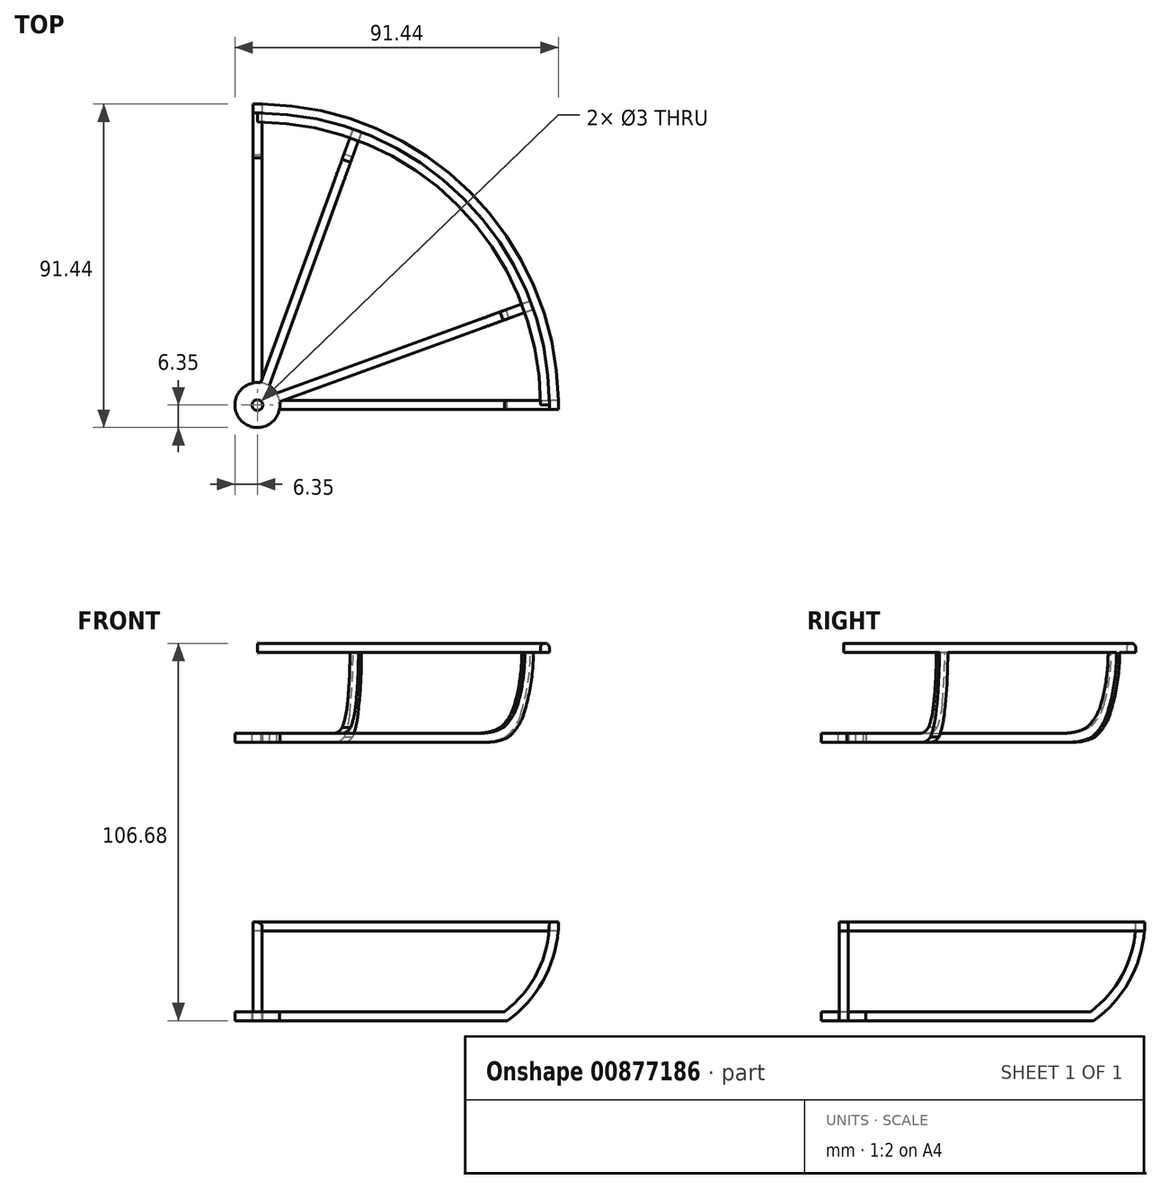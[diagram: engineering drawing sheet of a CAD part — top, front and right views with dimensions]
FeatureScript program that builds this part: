
annotation { "Feature Type Name" : "Feature", "Feature Type Description" : "" }
export const myFeature = defineFeature(function(context is Context, id is Id, definition is map)
    precondition{}
    {
        {
            var Q0;
            Q0=qCreatedBy(makeId("Front.planeOp"),FACE);
            var sketch = newSketch(context, id + "F0", { "sketchPlane" : qUnion([Q0])});
            skLineSegment(sketch, "E0", {"start": v(0, 0) * mm, "end": v(69.85, 0) * mm});
            skLineSegment(sketch, "E1.bottom", {"start": v(69.85, 0) * mm, "end": v(82.55, 0) * mm, "construction": true});
            skLineSegment(sketch, "E1.top", {"start": v(69.85, 25.4) * mm, "end": v(82.55, 25.4) * mm, "construction": true});
            skLineSegment(sketch, "E1.left", {"start": v(69.85, 0) * mm, "end": v(69.85, 25.4) * mm, "construction": true});
            skLineSegment(sketch, "E1.right", {"start": v(82.55, 0) * mm, "end": v(82.55, 25.4) * mm, "construction": true});
            skArc(sketch, "E2", {"start": v(69.85, 0) * mm, "mid": v(79.2, 11.2) * mm, "end": v(82.55, 25.4) * mm});
            skArc(sketch, "E3.0", {"start": v(70.68, -2.54) * mm, "mid": v(81.27, 9.68) * mm, "end": v(85.1, 25.4) * mm});
            skLineSegment(sketch, "E3.1", {"start": v(0, -2.54) * mm, "end": v(70.68, -2.54) * mm});
            skLineSegment(sketch, "E4", {"start": v(82.55, 25.4) * mm, "end": v(85.1, 25.4) * mm});
            skLineSegment(sketch, "E5", {"start": v(0, 0) * mm, "end": v(0, -2.54) * mm});
            skSolve(sketch);
        }
        {
            var Q0;
            Q0=qSketchRegion(id+"F0",true);
            extrude(context, id + "F1", {"entities" : qUnion([Q0]), "depth" : 2.54 * mm, "offsetDistance" : 25.4 * mm, "symmetric" : true});
        }
        {
            var Q0;
            Q0=qCreatedBy(makeId("Right.planeOp"),FACE);
            var sketch = newSketch(context, id + "F2", { "sketchPlane" : qUnion([Q0])});
            skLineSegment(sketch, "E6", {"start": v(0, 0) * mm, "end": v(69.85, 0) * mm});
            skLineSegment(sketch, "E7.bottom", {"start": v(69.85, 0) * mm, "end": v(82.55, 0) * mm, "construction": true});
            skLineSegment(sketch, "E7.top", {"start": v(69.85, 25.4) * mm, "end": v(82.55, 25.4) * mm, "construction": true});
            skLineSegment(sketch, "E7.left", {"start": v(69.85, 0) * mm, "end": v(69.85, 25.4) * mm, "construction": true});
            skLineSegment(sketch, "E7.right", {"start": v(82.55, 0) * mm, "end": v(82.55, 25.4) * mm, "construction": true});
            skArc(sketch, "E8", {"start": v(69.85, 0) * mm, "mid": v(79.2, 11.2) * mm, "end": v(82.55, 25.4) * mm});
            skArc(sketch, "E9.0", {"start": v(70.68, -2.54) * mm, "mid": v(81.27, 9.68) * mm, "end": v(85.1, 25.4) * mm});
            skLineSegment(sketch, "E9.1", {"start": v(0, -2.54) * mm, "end": v(70.68, -2.54) * mm});
            skLineSegment(sketch, "E10", {"start": v(82.55, 25.4) * mm, "end": v(85.1, 25.4) * mm});
            skLineSegment(sketch, "E11", {"start": v(0, 0) * mm, "end": v(0, -2.54) * mm});
            skSolve(sketch);
        }
        {
            var Q0;
            Q0=qSketchRegion(id+"F2",true);
            extrude(context, id + "F3", {"entities" : qUnion([Q0]), "operationType" : NewBodyOperationType.ADD, "depth" : 2.54 * mm, "offsetDistance" : 25.4 * mm, "symmetric" : true});
        }
        {
            var Q0;
            Q0=makeQuery(id+"F3.opExtrude","SWEPT_FACE",FACE,{"disambiguationData":[OSD([sQuery(id+"F2.wireOp",EDGE,"E10")])]});
            var sketch = newSketch(context, id + "F4", { "sketchPlane" : qUnion([Q0])});
            skPoint(sketch, "E12", {"position": v(0, 82.55) * mm});
            skLineSegment(sketch, "E13.bottom", {"start": v(0, 82.55) * mm, "end": v(82.55, 82.55) * mm, "construction": true});
            skLineSegment(sketch, "E13.top", {"start": v(0, 0) * mm, "end": v(82.55, 0) * mm, "construction": true});
            skLineSegment(sketch, "E13.left", {"start": v(0, 82.55) * mm, "end": v(0, 0) * mm, "construction": true});
            skLineSegment(sketch, "E13.right", {"start": v(82.55, 82.55) * mm, "end": v(82.55, 0) * mm, "construction": true});
            skArc(sketch, "E14", {"start": v(82.55, 0) * mm, "mid": v(58.37, 58.37) * mm, "end": v(0, 82.55) * mm});
            skArc(sketch, "E15.0", {"start": v(85.1, 0) * mm, "mid": v(60.17, 60.17) * mm, "end": v(0, 85.1) * mm});
            skLineSegment(sketch, "E16", {"start": v(82.55, 0) * mm, "end": v(83.82, 0) * mm, "construction": true});
            skLineSegment(sketch, "E17.bottom", {"start": v(85.1, -1.27) * mm, "end": v(82.55, -1.27) * mm});
            skLineSegment(sketch, "E17.top", {"start": v(85.1, 1.27) * mm, "end": v(82.55, 1.27) * mm});
            skLineSegment(sketch, "E17.left", {"start": v(85.1, -1.27) * mm, "end": v(85.1, 1.27) * mm});
            skLineSegment(sketch, "E17.right", {"start": v(82.55, -1.27) * mm, "end": v(82.55, 1.27) * mm});
            skPoint(sketch, "E17.middle", {"position": v(83.82, 0) * mm});
            skLineSegment(sketch, "E18", {"start": v(0, 82.55) * mm, "end": v(0, 83.82) * mm, "construction": true});
            skLineSegment(sketch, "E19.bottom", {"start": v(1.27, 85.1) * mm, "end": v(-1.27, 85.1) * mm});
            skLineSegment(sketch, "E19.top", {"start": v(1.27, 82.55) * mm, "end": v(-1.27, 82.55) * mm});
            skLineSegment(sketch, "E19.left", {"start": v(1.27, 85.1) * mm, "end": v(1.27, 82.55) * mm});
            skLineSegment(sketch, "E19.right", {"start": v(-1.27, 85.1) * mm, "end": v(-1.27, 82.55) * mm});
            skPoint(sketch, "E19.middle", {"position": v(0, 83.82) * mm});
            skSolve(sketch);
        }
        {
            var Q0;
            Q0=qSketchRegion(id+"F4",true);
            extrude(context, id + "F5", {"entities" : qUnion([Q0]), "operationType" : NewBodyOperationType.ADD, "oppositeDirection" : true, "depth" : 2.54 * mm, "offsetDistance" : 25.4 * mm});
        }
        {
            var Q0;
            Q0=qCreatedBy(makeId("Top.planeOp"),FACE);
            var sketch = newSketch(context, id + "F6", { "sketchPlane" : qUnion([Q0])});
            skCircle(sketch, "E20", {"center": v(0, 0) * mm, "radius": 6.35 * mm});
            skSolve(sketch);
        }
        {
            var Q0;
            Q0=qSketchRegion(id+"F6",true);
            extrude(context, id + "F7", {"entities" : qUnion([Q0]), "operationType" : NewBodyOperationType.ADD, "oppositeDirection" : true, "depth" : 2.54 * mm, "offsetDistance" : 25.4 * mm});
        }
        {
            var Q0;
            Q0=qCreatedBy(makeId("Top.planeOp"),FACE);
            var sketch = newSketch(context, id + "F8", { "sketchPlane" : qUnion([Q0])});
            skCircle(sketch, "E21", {"center": v(0, 0) * mm, "radius": 1.5 * mm});
            skSolve(sketch);
        }
        {
            var Q0;
            Q0=qSketchRegion(id+"F8",true);
            extrude(context, id + "F9", {"entities" : qUnion([Q0]), "operationType" : NewBodyOperationType.REMOVE, "oppositeDirection" : true, "depth" : 2.54 * mm, "offsetDistance" : 25.4 * mm});
        }
        {
            var Q0;
            Q0=makeQuery(id+"F5.boolean.opBoolean","MERGE",FACE,{"derivedFrom":[makeQuery(id+"F1.opExtrude","SWEPT_FACE",FACE,{"disambiguationData":[OSD([sQuery(id+"F0.wireOp",EDGE,"E4")])]}),makeQuery(id+"F3.opExtrude","SWEPT_FACE",FACE,{"disambiguationData":[OSD([sQuery(id+"F2.wireOp",EDGE,"E10")])]}),makeQuery(id+"F5.opExtrude","CAP_FACE",FACE,{"disambiguationData":[OSD([sQuery(id+"F4.wireOp",EDGE,"E14"),sQuery(id+"F4.wireOp",EDGE,"E15.0"),sQuery(id+"F4.wireOp",EDGE,"E17.bottom"),sQuery(id+"F4.wireOp",EDGE,"E17.top"),sQuery(id+"F4.wireOp",EDGE,"E17.left"),sQuery(id+"F4.wireOp",EDGE,"E17.right"),sQuery(id+"F4.wireOp",EDGE,"E19.bottom"),sQuery(id+"F4.wireOp",EDGE,"E19.top"),sQuery(id+"F4.wireOp",EDGE,"E19.left"),sQuery(id+"F4.wireOp",EDGE,"E19.right")])],"isStart":true})]});
            cPlane(context, id + "F10", {"entities" : qUnion([Q0]), "cplaneType" : CPlaneType.OFFSET, "offset" : 50.8 * mm, "width" : 152.4 * mm, "height" : 152.4 * mm});
        }
        {
            var Q0;
            Q0=qCreatedBy(id+"F10.planeOp",FACE);
            var sketch = newSketch(context, id + "F11", { "sketchPlane" : qUnion([Q0])});
            skCircle(sketch, "E22", {"center": v(0, 0) * mm, "radius": 6.35 * mm});
            skLineSegment(sketch, "E23", {"start": v(0, 0) * mm, "end": v(69.85, 0) * mm, "construction": true});
            skLineSegment(sketch, "E24", {"start": v(0, 0) * mm, "end": v(71.6, 26.06) * mm, "construction": true});
            skLineSegment(sketch, "E25", {"start": v(0, 0) * mm, "end": v(26.06, 71.6) * mm, "construction": true});
            skLineSegment(sketch, "E26.0", {"start": v(-2.12, -2.12) * mm, "end": v(72.04, 24.87) * mm});
            skLineSegment(sketch, "E26.1", {"start": v(-2.12, -2.12) * mm, "end": v(24.87, 72.04) * mm});
            skLineSegment(sketch, "E27.0", {"start": v(2.12, 2.12) * mm, "end": v(71.17, 27.26) * mm});
            skLineSegment(sketch, "E27.1", {"start": v(2.12, 2.12) * mm, "end": v(27.26, 71.17) * mm});
            skLineSegment(sketch, "E28", {"start": v(24.87, 72.04) * mm, "end": v(27.26, 71.17) * mm});
            skLineSegment(sketch, "E29", {"start": v(71.17, 27.26) * mm, "end": v(72.04, 24.87) * mm});
            skSolve(sketch);
        }
        {
            var Q0;
            Q0=qSketchRegion(id+"F11",true);
            extrude(context, id + "F12", {"entities" : qUnion([Q0]), "depth" : 2.54 * mm, "offsetDistance" : 25.4 * mm});
        }
        {
            var Q0;
            Q0=makeQuery(id+"F12.opExtrude","SWEPT_FACE",FACE,{"disambiguationData":[OSD([sQuery(id+"F11.wireOp",EDGE,"E26.0")])]});
            var sketch = newSketch(context, id + "F13", { "sketchPlane" : qUnion([Q0])});
            skLineSegment(sketch, "E30.bottom", {"start": v(76.2, 76.2) * mm, "end": v(82.55, 76.2) * mm, "construction": true});
            skLineSegment(sketch, "E30.top", {"start": v(76.2, 101.6) * mm, "end": v(82.55, 101.6) * mm, "construction": true});
            skLineSegment(sketch, "E30.left", {"start": v(76.2, 76.2) * mm, "end": v(76.2, 101.6) * mm, "construction": true});
            skLineSegment(sketch, "E30.right", {"start": v(82.55, 76.2) * mm, "end": v(82.55, 101.6) * mm, "construction": true});
            skArc(sketch, "E31", {"start": v(76.2, 76.2) * mm, "mid": v(80.94, 88.5) * mm, "end": v(82.55, 101.6) * mm});
            skArc(sketch, "E32.0", {"start": v(73.96, 77.4) * mm, "mid": v(78.47, 89.13) * mm, "end": v(80.01, 101.6) * mm});
            skLineSegment(sketch, "E33", {"start": v(73.96, 77.4) * mm, "end": v(76.2, 76.2) * mm});
            skLineSegment(sketch, "E34", {"start": v(82.55, 101.6) * mm, "end": v(80.01, 101.6) * mm});
            skSolve(sketch);
        }
        {
            var Q0;
            Q0=qSketchRegion(id+"F13",true);
            extrude(context, id + "F14", {"entities" : qUnion([Q0]), "operationType" : NewBodyOperationType.ADD, "oppositeDirection" : true, "depth" : 2.54 * mm, "offsetDistance" : 25.4 * mm});
        }
        {
            var Q0;
            Q0=makeQuery(id+"F12.opExtrude","SWEPT_FACE",FACE,{"disambiguationData":[OSD([sQuery(id+"F11.wireOp",EDGE,"E27.1")])]});
            var sketch = newSketch(context, id + "F15", { "sketchPlane" : qUnion([Q0])});
            skLineSegment(sketch, "E35.bottom", {"start": v(76.2, 76.2) * mm, "end": v(82.55, 76.2) * mm, "construction": true});
            skLineSegment(sketch, "E35.top", {"start": v(76.2, 101.6) * mm, "end": v(82.55, 101.6) * mm, "construction": true});
            skLineSegment(sketch, "E35.left", {"start": v(76.2, 76.2) * mm, "end": v(76.2, 101.6) * mm, "construction": true});
            skLineSegment(sketch, "E35.right", {"start": v(82.55, 76.2) * mm, "end": v(82.55, 101.6) * mm, "construction": true});
            skArc(sketch, "E36", {"start": v(76.2, 76.2) * mm, "mid": v(80.94, 88.5) * mm, "end": v(82.55, 101.6) * mm});
            skArc(sketch, "E37.0", {"start": v(73.96, 77.4) * mm, "mid": v(78.47, 89.13) * mm, "end": v(80.01, 101.6) * mm});
            skLineSegment(sketch, "E38", {"start": v(73.96, 77.4) * mm, "end": v(76.2, 76.2) * mm});
            skLineSegment(sketch, "E39", {"start": v(82.55, 101.6) * mm, "end": v(80.01, 101.6) * mm});
            skSolve(sketch);
        }
        {
            var Q0;
            Q0=qSketchRegion(id+"F15",true);
            extrude(context, id + "F16", {"entities" : qUnion([Q0]), "operationType" : NewBodyOperationType.ADD, "oppositeDirection" : true, "depth" : 2.54 * mm, "offsetDistance" : 25.4 * mm});
        }
        {
            var Q0;
            Q0=makeQuery(id+"F16.opExtrude","SWEPT_FACE",FACE,{"disambiguationData":[OSD([sQuery(id+"F15.wireOp",EDGE,"E39")])]});
            var sketch = newSketch(context, id + "F17", { "sketchPlane" : qUnion([Q0])});
            skLineSegment(sketch, "E40", {"start": v(0, 0) * mm, "end": v(0, 80.01) * mm, "construction": true});
            skLineSegment(sketch, "E41", {"start": v(0, 0) * mm, "end": v(80.01, 0) * mm, "construction": true});
            skArc(sketch, "E42", {"start": v(80.01, 0) * mm, "mid": v(56.58, 56.58) * mm, "end": v(0, 80.01) * mm});
            skArc(sketch, "E43.0", {"start": v(82.55, 0) * mm, "mid": v(58.37, 58.37) * mm, "end": v(0, 82.55) * mm});
            skLineSegment(sketch, "E44", {"start": v(0, 80.01) * mm, "end": v(0, 82.55) * mm});
            skLineSegment(sketch, "E45", {"start": v(80.01, 0) * mm, "end": v(82.55, 0) * mm});
            skSolve(sketch);
        }
        {
            var Q0;
            Q0=qSketchRegion(id+"F17",true);
            extrude(context, id + "F18", {"entities" : qUnion([Q0]), "operationType" : NewBodyOperationType.ADD, "depth" : 2.54 * mm, "offsetDistance" : 25.4 * mm});
        }
        {
            var Q0;
            Q0=makeQuery(id+"F12.opExtrude","CAP_FACE",FACE,{"disambiguationData":[OSD([sQuery(id+"F11.wireOp",EDGE,"E22"),sQuery(id+"F11.wireOp",EDGE,"E26.0"),sQuery(id+"F11.wireOp",EDGE,"E26.1"),sQuery(id+"F11.wireOp",EDGE,"E27.0"),sQuery(id+"F11.wireOp",EDGE,"E27.1"),sQuery(id+"F11.wireOp",EDGE,"E28"),sQuery(id+"F11.wireOp",EDGE,"E29")])],"isStart":false});
            var sketch = newSketch(context, id + "F19", { "sketchPlane" : qUnion([Q0])});
            skCircle(sketch, "E46", {"center": v(0, 0) * mm, "radius": 1.5 * mm});
            skSolve(sketch);
        }
        {
            var Q0;
            Q0=qSketchRegion(id+"F19",true);
            extrude(context, id + "F20", {"entities" : qUnion([Q0]), "operationType" : NewBodyOperationType.REMOVE, "oppositeDirection" : true, "depth" : 2.54 * mm, "offsetDistance" : 25.4 * mm});
        }
        {
            var Q0;
            Q0=makeQuery(id+"F14.boolean.opBoolean","INTERSECT",EDGE,{"derivedFrom":[makeQuery(id+"F12.opExtrude","CAP_FACE",FACE,{"disambiguationData":[OSD([sQuery(id+"F11.wireOp",EDGE,"E22"),sQuery(id+"F11.wireOp",EDGE,"E26.0"),sQuery(id+"F11.wireOp",EDGE,"E26.1"),sQuery(id+"F11.wireOp",EDGE,"E27.0"),sQuery(id+"F11.wireOp",EDGE,"E27.1"),sQuery(id+"F11.wireOp",EDGE,"E28"),sQuery(id+"F11.wireOp",EDGE,"E29")])],"isStart":false}),makeQuery(id+"F14.opExtrude","SWEPT_FACE",FACE,{"disambiguationData":[OSD([sQuery(id+"F13.wireOp",EDGE,"E32.0")])]})]});
            var Q1;
            Q1=makeQuery(id+"F16.boolean.opBoolean","INTERSECT",EDGE,{"derivedFrom":[makeQuery(id+"F12.opExtrude","CAP_FACE",FACE,{"disambiguationData":[OSD([sQuery(id+"F11.wireOp",EDGE,"E22"),sQuery(id+"F11.wireOp",EDGE,"E26.0"),sQuery(id+"F11.wireOp",EDGE,"E26.1"),sQuery(id+"F11.wireOp",EDGE,"E27.0"),sQuery(id+"F11.wireOp",EDGE,"E27.1"),sQuery(id+"F11.wireOp",EDGE,"E28"),sQuery(id+"F11.wireOp",EDGE,"E29")])],"isStart":false}),makeQuery(id+"F16.opExtrude","SWEPT_FACE",FACE,{"disambiguationData":[OSD([sQuery(id+"F15.wireOp",EDGE,"E37.0")])]})]});
            var Q2;
            {var subQ0=sQuery(id+"F11.wireOp",EDGE,"E28");Q2=makeQuery(id+"F16.boolean.opBoolean","MERGE",EDGE,{"derivedFrom":[makeQuery(id+"F12.opExtrude","CAP_EDGE",EDGE,{"disambiguationData":[OSD([subQ0])],"isStart":true}),makeQuery(id+"F16.opExtrude","SWEPT_EDGE",EDGE,{"disambiguationData":[OSD([sQuery(id+"F11.wireOp",EDGE,"E27.1"),subQ0,sQuery(id+"F15.wireOp",EDGE,"E36"),sQuery(id+"F15.wireOp",EDGE,"E38")])]})]});}
            var Q3;
            {var subQ0=sQuery(id+"F11.wireOp",EDGE,"E29");Q3=makeQuery(id+"F14.boolean.opBoolean","MERGE",EDGE,{"derivedFrom":[makeQuery(id+"F12.opExtrude","CAP_EDGE",EDGE,{"disambiguationData":[OSD([subQ0])],"isStart":true}),makeQuery(id+"F14.opExtrude","SWEPT_EDGE",EDGE,{"disambiguationData":[OSD([sQuery(id+"F11.wireOp",EDGE,"E26.0"),subQ0,sQuery(id+"F13.wireOp",EDGE,"E31"),sQuery(id+"F13.wireOp",EDGE,"E33")])]})]});}
            chamfer(context, id + "F21", {"entities" : qUnion([Q0, Q1, Q2, Q3]), "width" : 5.08 * mm, "tangentPropagation" : true});
        }
        {
            var Q0;
            {var subQ0=sQuery(id+"F13.wireOp",EDGE,"E31");var subQ1=sQuery(id+"F11.wireOp",EDGE,"E29");Q0=makeQuery(id+"F21.opChamfer","BLEND_EDGE",EDGE,{"blendedFrom":[makeQuery(id+"F14.boolean.opBoolean","MERGE",EDGE,{"derivedFrom":[makeQuery(id+"F12.opExtrude","CAP_EDGE",EDGE,{"disambiguationData":[OSD([subQ1])],"isStart":true}),makeQuery(id+"F14.opExtrude","SWEPT_EDGE",EDGE,{"disambiguationData":[OSD([sQuery(id+"F11.wireOp",EDGE,"E26.0"),subQ1,subQ0,sQuery(id+"F13.wireOp",EDGE,"E33")])]})]}),makeQuery(id+"F14.opExtrude","SWEPT_FACE",FACE,{"disambiguationData":[OSD([subQ0])]})],"blendedInto":[makeQuery(id+"F14.opExtrude","SWEPT_FACE",FACE,{"disambiguationData":[OSD([subQ0])]})]});}
            var Q1;
            {var subQ0=sQuery(id+"F11.wireOp",EDGE,"E29");var subQ1=sQuery(id+"F11.wireOp",EDGE,"E26.0");Q1=makeQuery(id+"F21.opChamfer","BLEND_EDGE",EDGE,{"blendedFrom":[makeQuery(id+"F14.boolean.opBoolean","MERGE",EDGE,{"derivedFrom":[makeQuery(id+"F12.opExtrude","CAP_EDGE",EDGE,{"disambiguationData":[OSD([subQ0])],"isStart":true}),makeQuery(id+"F14.opExtrude","SWEPT_EDGE",EDGE,{"disambiguationData":[OSD([subQ1,subQ0,sQuery(id+"F13.wireOp",EDGE,"E31"),sQuery(id+"F13.wireOp",EDGE,"E33")])]})]}),makeQuery(id+"F12.opExtrude","CAP_FACE",FACE,{"disambiguationData":[OSD([sQuery(id+"F11.wireOp",EDGE,"E22"),subQ1,sQuery(id+"F11.wireOp",EDGE,"E26.1"),sQuery(id+"F11.wireOp",EDGE,"E27.0"),sQuery(id+"F11.wireOp",EDGE,"E27.1"),sQuery(id+"F11.wireOp",EDGE,"E28"),subQ0])],"isStart":true})],"blendedInto":[makeQuery(id+"F12.opExtrude","CAP_FACE",FACE,{"disambiguationData":[OSD([sQuery(id+"F11.wireOp",EDGE,"E22"),subQ1,sQuery(id+"F11.wireOp",EDGE,"E26.1"),sQuery(id+"F11.wireOp",EDGE,"E27.0"),sQuery(id+"F11.wireOp",EDGE,"E27.1"),sQuery(id+"F11.wireOp",EDGE,"E28"),subQ0])],"isStart":true})]});}
            var Q2;
            {var subQ0=makeQuery(id+"F14.opExtrude","SWEPT_FACE",FACE,{"disambiguationData":[OSD([sQuery(id+"F13.wireOp",EDGE,"E32.0")])]});Q2=makeQuery(id+"F21.opChamfer","BLEND_EDGE",EDGE,{"blendedFrom":[makeQuery(id+"F14.boolean.opBoolean","INTERSECT",EDGE,{"derivedFrom":[makeQuery(id+"F12.opExtrude","CAP_FACE",FACE,{"disambiguationData":[OSD([sQuery(id+"F11.wireOp",EDGE,"E22"),sQuery(id+"F11.wireOp",EDGE,"E26.0"),sQuery(id+"F11.wireOp",EDGE,"E26.1"),sQuery(id+"F11.wireOp",EDGE,"E27.0"),sQuery(id+"F11.wireOp",EDGE,"E27.1"),sQuery(id+"F11.wireOp",EDGE,"E28"),sQuery(id+"F11.wireOp",EDGE,"E29")])],"isStart":false}),subQ0]}),subQ0],"blendedInto":[subQ0]});}
            var Q3;
            {var subQ0=makeQuery(id+"F12.opExtrude","CAP_FACE",FACE,{"disambiguationData":[OSD([sQuery(id+"F11.wireOp",EDGE,"E22"),sQuery(id+"F11.wireOp",EDGE,"E26.0"),sQuery(id+"F11.wireOp",EDGE,"E26.1"),sQuery(id+"F11.wireOp",EDGE,"E27.0"),sQuery(id+"F11.wireOp",EDGE,"E27.1"),sQuery(id+"F11.wireOp",EDGE,"E28"),sQuery(id+"F11.wireOp",EDGE,"E29")])],"isStart":false});Q3=makeQuery(id+"F21.opChamfer","BLEND_EDGE",EDGE,{"blendedFrom":[makeQuery(id+"F14.boolean.opBoolean","INTERSECT",EDGE,{"derivedFrom":[subQ0,makeQuery(id+"F14.opExtrude","SWEPT_FACE",FACE,{"disambiguationData":[OSD([sQuery(id+"F13.wireOp",EDGE,"E32.0")])]})]}),subQ0],"blendedInto":[subQ0]});}
            var Q4;
            {var subQ0=makeQuery(id+"F12.opExtrude","CAP_FACE",FACE,{"disambiguationData":[OSD([sQuery(id+"F11.wireOp",EDGE,"E22"),sQuery(id+"F11.wireOp",EDGE,"E26.0"),sQuery(id+"F11.wireOp",EDGE,"E26.1"),sQuery(id+"F11.wireOp",EDGE,"E27.0"),sQuery(id+"F11.wireOp",EDGE,"E27.1"),sQuery(id+"F11.wireOp",EDGE,"E28"),sQuery(id+"F11.wireOp",EDGE,"E29")])],"isStart":false});Q4=makeQuery(id+"F21.opChamfer","BLEND_EDGE",EDGE,{"blendedFrom":[makeQuery(id+"F16.boolean.opBoolean","INTERSECT",EDGE,{"derivedFrom":[subQ0,makeQuery(id+"F16.opExtrude","SWEPT_FACE",FACE,{"disambiguationData":[OSD([sQuery(id+"F15.wireOp",EDGE,"E37.0")])]})]}),subQ0],"blendedInto":[subQ0]});}
            var Q5;
            {var subQ0=makeQuery(id+"F16.opExtrude","SWEPT_FACE",FACE,{"disambiguationData":[OSD([sQuery(id+"F15.wireOp",EDGE,"E37.0")])]});Q5=makeQuery(id+"F21.opChamfer","BLEND_EDGE",EDGE,{"blendedFrom":[makeQuery(id+"F16.boolean.opBoolean","INTERSECT",EDGE,{"derivedFrom":[makeQuery(id+"F12.opExtrude","CAP_FACE",FACE,{"disambiguationData":[OSD([sQuery(id+"F11.wireOp",EDGE,"E22"),sQuery(id+"F11.wireOp",EDGE,"E26.0"),sQuery(id+"F11.wireOp",EDGE,"E26.1"),sQuery(id+"F11.wireOp",EDGE,"E27.0"),sQuery(id+"F11.wireOp",EDGE,"E27.1"),sQuery(id+"F11.wireOp",EDGE,"E28"),sQuery(id+"F11.wireOp",EDGE,"E29")])],"isStart":false}),subQ0]}),subQ0],"blendedInto":[subQ0]});}
            var Q6;
            {var subQ0=sQuery(id+"F15.wireOp",EDGE,"E36");var subQ1=sQuery(id+"F11.wireOp",EDGE,"E28");Q6=makeQuery(id+"F21.opChamfer","BLEND_EDGE",EDGE,{"blendedFrom":[makeQuery(id+"F16.boolean.opBoolean","MERGE",EDGE,{"derivedFrom":[makeQuery(id+"F12.opExtrude","CAP_EDGE",EDGE,{"disambiguationData":[OSD([subQ1])],"isStart":true}),makeQuery(id+"F16.opExtrude","SWEPT_EDGE",EDGE,{"disambiguationData":[OSD([sQuery(id+"F11.wireOp",EDGE,"E27.1"),subQ1,subQ0,sQuery(id+"F15.wireOp",EDGE,"E38")])]})]}),makeQuery(id+"F16.opExtrude","SWEPT_FACE",FACE,{"disambiguationData":[OSD([subQ0])]})],"blendedInto":[makeQuery(id+"F16.opExtrude","SWEPT_FACE",FACE,{"disambiguationData":[OSD([subQ0])]})]});}
            var Q7;
            {var subQ0=sQuery(id+"F11.wireOp",EDGE,"E28");var subQ1=sQuery(id+"F11.wireOp",EDGE,"E27.1");Q7=makeQuery(id+"F21.opChamfer","BLEND_EDGE",EDGE,{"blendedFrom":[makeQuery(id+"F16.boolean.opBoolean","MERGE",EDGE,{"derivedFrom":[makeQuery(id+"F12.opExtrude","CAP_EDGE",EDGE,{"disambiguationData":[OSD([subQ0])],"isStart":true}),makeQuery(id+"F16.opExtrude","SWEPT_EDGE",EDGE,{"disambiguationData":[OSD([subQ1,subQ0,sQuery(id+"F15.wireOp",EDGE,"E36"),sQuery(id+"F15.wireOp",EDGE,"E38")])]})]}),makeQuery(id+"F12.opExtrude","CAP_FACE",FACE,{"disambiguationData":[OSD([sQuery(id+"F11.wireOp",EDGE,"E22"),sQuery(id+"F11.wireOp",EDGE,"E26.0"),sQuery(id+"F11.wireOp",EDGE,"E26.1"),sQuery(id+"F11.wireOp",EDGE,"E27.0"),subQ1,subQ0,sQuery(id+"F11.wireOp",EDGE,"E29")])],"isStart":true})],"blendedInto":[makeQuery(id+"F12.opExtrude","CAP_FACE",FACE,{"disambiguationData":[OSD([sQuery(id+"F11.wireOp",EDGE,"E22"),sQuery(id+"F11.wireOp",EDGE,"E26.0"),sQuery(id+"F11.wireOp",EDGE,"E26.1"),sQuery(id+"F11.wireOp",EDGE,"E27.0"),subQ1,subQ0,sQuery(id+"F11.wireOp",EDGE,"E29")])],"isStart":true})]});}
            fillet(context, id + "F22", {"entities" : qUnion([Q0, Q1, Q2, Q3, Q4, Q5, Q6, Q7]), "radius" : 14.22 * mm, "tangentPropagation" : true, "allowEdgeOverflow" : false});
        }
        {
            var Q0;
            Q0=makeQuery(id+"F18.opExtrude","CAP_EDGE",EDGE,{"disambiguationData":[OSD([sQuery(id+"F17.wireOp",EDGE,"E42")])],"isStart":false});
            var Q1;
            Q1=makeQuery(id+"F18.opExtrude","CAP_EDGE",EDGE,{"disambiguationData":[OSD([sQuery(id+"F17.wireOp",EDGE,"E43.0")])],"isStart":false});
            fillet(context, id + "F23", {"entities" : qUnion([Q0, Q1]), "radius" : 1.27 * mm, "tangentPropagation" : true, "allowEdgeOverflow" : false});
        }
    });
